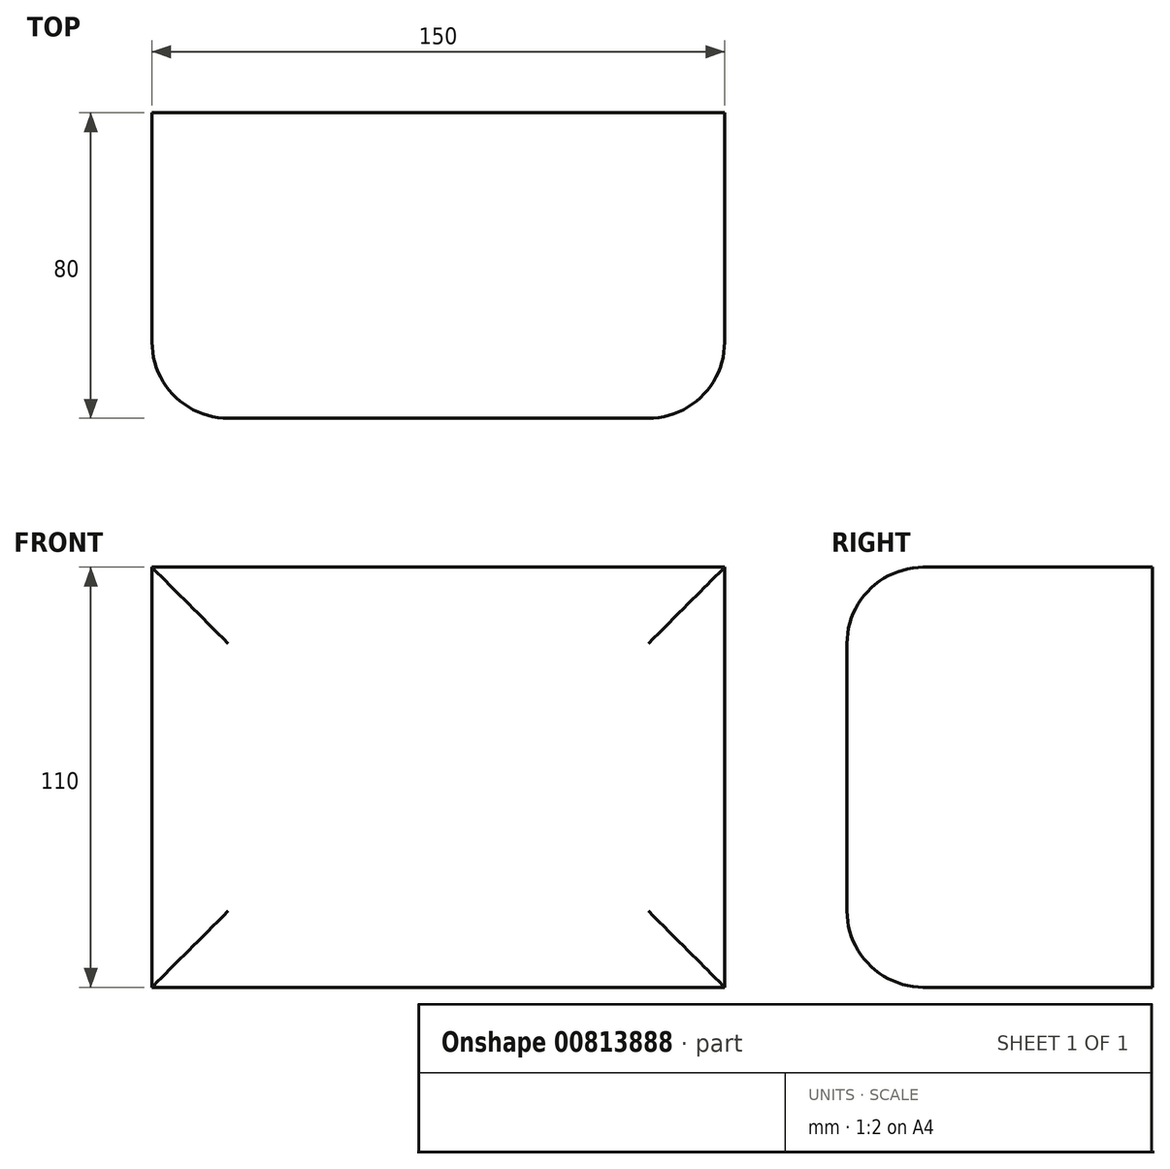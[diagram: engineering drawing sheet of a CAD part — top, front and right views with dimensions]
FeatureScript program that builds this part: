
annotation { "Feature Type Name" : "Feature", "Feature Type Description" : "" }
export const myFeature = defineFeature(function(context is Context, id is Id, definition is map)
    precondition{}
    {
        {
            var Q0;
            Q0=qCreatedBy(makeId("Front.planeOp"),FACE);
            var sketch = newSketch(context, id + "F0", { "sketchPlane" : qUnion([Q0])});
            skLineSegment(sketch, "E0.bottom", {"start": v(-75, -55) * mm, "end": v(75, -55) * mm});
            skLineSegment(sketch, "E0.top", {"start": v(-75, 55) * mm, "end": v(75, 55) * mm});
            skLineSegment(sketch, "E0.left", {"start": v(-75, -55) * mm, "end": v(-75, 55) * mm});
            skLineSegment(sketch, "E0.right", {"start": v(75, -55) * mm, "end": v(75, 55) * mm});
            skPoint(sketch, "E0.middle", {"position": v(0, 0) * mm});
            skSolve(sketch);
        }
        {
            var Q0;
            Q0 = qSketchRegion(id + "F0", true);
            extrude(context, id + "F1", {"entities" : qUnion([Q0]), "depth" : 80 * mm, "offsetDistance" : 25.4 * mm});
        }
        {
            var Q0;
            Q0=makeQuery(id+"F1.opExtrude","CAP_EDGE",EDGE,{"disambiguationData":[OSD([sQuery(id+"F0.wireOp",EDGE,"E0.top")])],"isStart":false});
            var Q1;
            Q1=makeQuery(id+"F1.opExtrude","CAP_EDGE",EDGE,{"disambiguationData":[OSD([sQuery(id+"F0.wireOp",EDGE,"E0.left")])],"isStart":false});
            var Q2;
            Q2=makeQuery(id+"F1.opExtrude","CAP_EDGE",EDGE,{"disambiguationData":[OSD([sQuery(id+"F0.wireOp",EDGE,"E0.bottom")])],"isStart":false});
            var Q3;
            Q3=makeQuery(id+"F1.opExtrude","CAP_EDGE",EDGE,{"disambiguationData":[OSD([sQuery(id+"F0.wireOp",EDGE,"E0.right")])],"isStart":false});
            fillet(context, id + "F2", {"entities" : qUnion([Q0, Q1, Q2, Q3]), "radius" : 20 * mm, "tangentPropagation" : true, "allowEdgeOverflow" : false});
        }
    });
